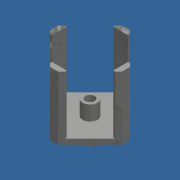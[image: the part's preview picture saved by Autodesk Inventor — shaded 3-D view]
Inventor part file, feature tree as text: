
AUTODESK INVENTOR PART (.ipt)
format: ipt  version: 2020 (Build 240168000, 168)  size: 2,219,520 bytes
history: mixed  units: mm
features: sketch x5, extrude x4, hole x1, pattern_circular x1, chamfer x1, fillet x1, imported_body x1
ambient origin geometry x8: Origin, YZ Plane, XZ Plane, XY Plane, X Axis, Y Axis, Z Axis, Center Point
bodies: Solid1 (imported_parasolid)
feature tree (14):
  extrude  "Extrusion1"  Depth=4.0mm TaperAngle=0.0deg
  extrude  "Extrusion3"  Depth=68.0mm
  extrude  "Extrusion4"  Depth=14.0mm
  extrude  "Extrusion5"  Depth=5.0mm
  hole  "Hole6"  [1 undecoded]
  pattern_circular  "Circular Pattern2"  [2 undecoded]
  chamfer  "Chamfer2"  Distance=14.0mm
  sketch  "Sketch1"  dims[d0=35.0mm d1=4.0mm d2=0.0mm]
  sketch  "Sketch4"  dims[d42=68.0mm d43=68.0mm]
  sketch  "Sketch5"  dims[d44=5.0mm d45=0.0mm d46=14.0mm]
  sketch  "Sketch7"  dims[d47=5.0mm d48=29.0mm]
  sketch  "Sketch8"  dims[d49=7.0mm d50=55.0mm d51=0.0mm d69=4.0mm d70=0.0mm d78=14.0mm d79=14.0mm d80=0.0mm d81=8.5mm d82=6.0mm d83=4.0mm d84=2.0mm d85=90.0deg d86=51.6mm d87=0.0mm d88=40.0mm d89=360.0deg d91=30.0mm d92=2.0mm d93=45.0deg]
  fillet  "Redondeo2"  Radius=14.0mm
  imported_body  NMx_Import_Brep_tag  [imported B-rep: ~996 faces, bbox_mm=[68.0, 68.0, 68.0]]
note: 3 required parameter values undecoded (feature->parameter linkage not recoverable at this tier; creation-order binding heuristic only, values carry confidence <= 0.55)
